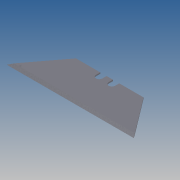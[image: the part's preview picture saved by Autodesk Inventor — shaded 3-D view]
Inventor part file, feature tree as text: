
AUTODESK INVENTOR PART (.ipt)
format: ipt  version: 2012 (Build 160160000, 160)  size: 93,696 bytes
history: native  units: mm
features: chamfer x2, extrude x1, sketch x1
ambient origin geometry x8: Origin, YZ Plane, XZ Plane, XY Plane, X Axis, Y Axis, Z Axis, Center Point
bodies: Solid1 (feature_tree)
feature tree (4):
  extrude  "Extrusion1"  Depth=18.7mm
  chamfer  "Chamfer1"  Distance=16.0mm
  chamfer  "Chamfer2"  Distance=3.0mm
  sketch  "Sketch1"  dims[d0=0.0mm d1=18.7mm d4=16.0mm d6=3.0mm d8=2.0mm d9=0.6mm d10=0.0mm d11=0.3mm d12=2.0mm d13=45.0deg d14=0.3mm d15=2.0mm d16=45.0deg]
